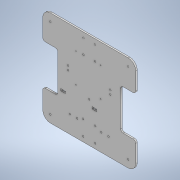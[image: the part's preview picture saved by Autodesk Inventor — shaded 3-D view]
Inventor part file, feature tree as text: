
AUTODESK INVENTOR PART (.ipt)
format: ipt  version: 2020 (Build 240168000, 168)  size: 188,928 bytes
history: native  units: in
note: dims shown in document units (in); Inventor stores cm internally (conversion verified against a paired STEP export)
features: fillet x2, extrude x1, sketch x1
ambient origin geometry x8: Origin, YZ Plane, XZ Plane, XY Plane, X Axis, Y Axis, Z Axis, Center Point
bodies: Solid1 (feature_tree)
feature tree (4):
  extrude  "Extrusion1"  Depth=0.5906in
  fillet  "Fillet1"  Radius=0.1969in
  fillet  "Fillet2"  [1 undecoded]
  sketch  "Sketch1"  dims[d0=0.1181in d1=0.0in d2=0.5906in d3=0.1969in]
note: 1 required parameter value undecoded (feature->parameter linkage not recoverable at this tier; creation-order binding heuristic only, values carry confidence <= 0.55)
